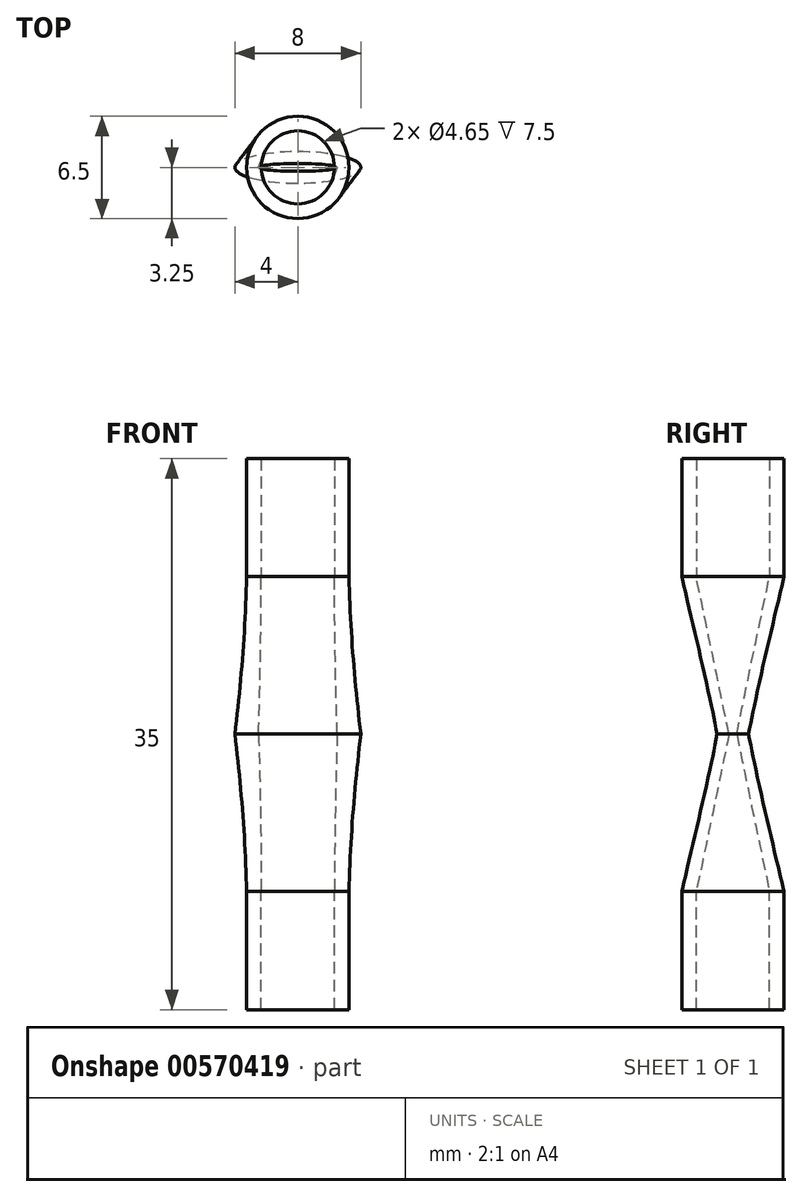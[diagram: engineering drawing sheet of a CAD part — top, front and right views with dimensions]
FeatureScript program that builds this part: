
annotation { "Feature Type Name" : "Feature", "Feature Type Description" : "" }
export const myFeature = defineFeature(function(context is Context, id is Id, definition is map)
    precondition{}
    {
        {
            var Q0;
            Q0=qCreatedBy(makeId("Top.planeOp"),FACE);
            var sketch = newSketch(context, id + "F0", { "sketchPlane" : qUnion([Q0])});
            skCircle(sketch, "E0", {"center": v(0, 0) * mm, "radius": 3.25 * mm});
            skCircle(sketch, "E1", {"center": v(0, 0) * mm, "radius": 2.33 * mm});
            skSolve(sketch);
        }
        {
            var Q0;
            Q0=qCreatedBy(makeId("Top.planeOp"),FACE);
            var sketch = newSketch(context, id + "F1", { "sketchPlane" : qUnion([Q0])});
            skCircle(sketch, "E2.0", {"center": v(0, 0) * mm, "radius": 3.25 * mm});
            skSolve(sketch);
        }
        {
            var Q0;
            Q0=qCreatedBy(makeId("Top.planeOp"),FACE);
            cPlane(context, id + "F2", {"entities" : qUnion([Q0]), "cplaneType" : CPlaneType.OFFSET, "offset" : 10 * mm, "width" : 150 * mm, "height" : 150 * mm});
        }
        {
            var Q0;
            Q0=qCreatedBy(id+"F2.planeOp",FACE);
            var sketch = newSketch(context, id + "F3", { "sketchPlane" : qUnion([Q0])});
            skCircle(sketch, "E3", {"center": v(0, 0) * mm, "radius": 1 * mm, "construction": true});
            skCircle(sketch, "E4", {"center": v(0, 0) * mm, "radius": 4 * mm, "construction": true});
            skEllipse(sketch, "E5", {"center": v(0, 0) * mm, "majorRadius": 4 * mm, "minorRadius": 1 * mm, "majorAxis": v(-1, 0)});
            skEllipse(sketch, "E6", {"center": v(0, 0) * mm, "majorRadius": 2.5 * mm, "minorRadius": 0.25 * mm, "majorAxis": v(-1, 0)});
            skSolve(sketch);
        }
        {
            var Q0;
            Q0=qCreatedBy(id+"F2.planeOp",FACE);
            var sketch = newSketch(context, id + "F4", { "sketchPlane" : qUnion([Q0])});
            skEllipse(sketch, "E7.0", {"center": v(0, 0) * mm, "majorRadius": 4 * mm, "minorRadius": 1 * mm, "majorAxis": v(-1, 0)});
            skSolve(sketch);
        }
        {
            var Q0;
            Q0=makeQuery(id+"F1.imprint","IMPRINT",FACE,{"disambiguationData":[TD([[makeQuery(id+"F1.imprint","IMPRINT",EDGE,{"derivedFrom":sQuery(id+"F1.wireOp",EDGE,"E2.0")}),1.0]])]});
            var Q1;
            Q1=makeQuery(id+"F4.imprint","IMPRINT",FACE,{"disambiguationData":[TD([[makeQuery(id+"F4.imprint","IMPRINT",EDGE,{"derivedFrom":sQuery(id+"F4.wireOp",EDGE,"E7.0")}),1.0]])]});
            loft(context, id + "F5", {"sheetProfilesArray" : [{ "sheetProfileEntities" : qUnion([Q0]) }, { "sheetProfileEntities" : qUnion([Q1]) }]});
        }
        {
            var Q0;
            Q0=makeQuery(id+"F0.imprint","IMPRINT",FACE,{"disambiguationData":[TD([[makeQuery(id+"F0.imprint","IMPRINT",EDGE,{"derivedFrom":sQuery(id+"F0.wireOp",EDGE,"E1")}),1.0]])]});
            var Q1;
            Q1=makeQuery(id+"F3.imprint","IMPRINT",FACE,{"disambiguationData":[TD([[makeQuery(id+"F3.imprint","IMPRINT",EDGE,{"derivedFrom":sQuery(id+"F3.wireOp",EDGE,"E6")}),1.0]])]});
            loft(context, id + "F6", {"operationType" : NewBodyOperationType.REMOVE, "sheetProfilesArray" : [{ "sheetProfileEntities" : qUnion([Q0]) }, { "sheetProfileEntities" : qUnion([Q1]) }]});
        }
        {
            var Q0;
            Q0=makeQuery(id+"F5.opLoft","CAP_FACE",FACE,{"disambiguationData":[OSD([makeQuery(id+"F1.imprint","IMPRINT",FACE,{"disambiguationData":[TD([[makeQuery(id+"F1.imprint","IMPRINT",EDGE,{"derivedFrom":sQuery(id+"F1.wireOp",EDGE,"E2.0")}),1.0]])]})])],"isStart":true});
            extrude(context, id + "F7", {"entities" : qUnion([Q0]), "operationType" : NewBodyOperationType.ADD, "depth" : 7.5 * mm, "offsetDistance" : 25 * mm});
        }
        {
            var Q0;
            Q0=makeQuery(id+"F5.opLoft","SWEPT_BODY",BODY,{"disambiguationData":[OSD([makeQuery(id+"F1.imprint","IMPRINT",FACE,{"disambiguationData":[TD([[makeQuery(id+"F1.imprint","IMPRINT",EDGE,{"derivedFrom":sQuery(id+"F1.wireOp",EDGE,"E2.0")}),1.0]])]}),makeQuery(id+"F4.imprint","IMPRINT",FACE,{"disambiguationData":[TD([[makeQuery(id+"F4.imprint","IMPRINT",EDGE,{"derivedFrom":sQuery(id+"F4.wireOp",EDGE,"E7.0")}),1.0]])]})])]});
            var Q1;
            Q1=qCreatedBy(id+"F2.planeOp",FACE);
            mirror(context, id + "F8", {"operationType" : NewBodyOperationType.ADD, "entities" : qUnion([Q0]), "mirrorPlane" : qUnion([Q1])});
        }
    });
